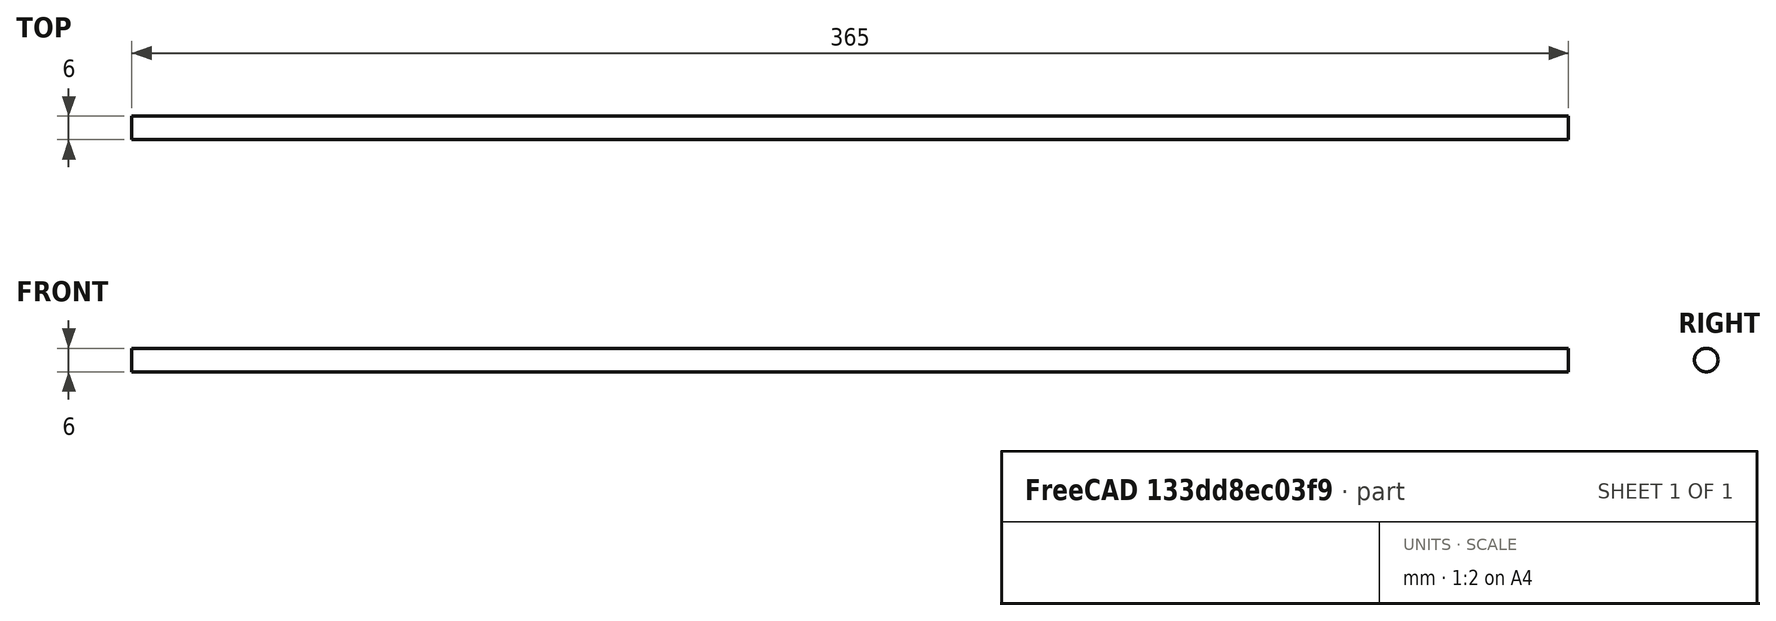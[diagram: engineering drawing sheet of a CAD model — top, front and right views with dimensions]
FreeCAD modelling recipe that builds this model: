
FCSTD DOCUMENT  (FreeCAD 0.18R15441 (Git))
Label: Rod_M6x365mm
License: All rights reserved
LicenseURL: http://en.wikipedia.org/wiki/All_rights_reserved
objects: Sketcher::SketchObject×1, PartDesign::Pad×1, PartDesign::Body×1, App::Part×1
note: 4 computed .brp shape members not serialized (recipe doc carries the construction recipe); baked Part::Feature solids carry a one-line shape summary decoded from their .brp

FEATURE [Sketcher::SketchObject] Sketch  label="RodSketch"
  MapMode = 5
  Placement = pos=(0,0,0) rot=(0.57735,0.57735,0.57735;2.0944rad)
  Support = -> [YZ_Plane001]
  sketch-geometry (1):
    g0: Circle CenterX=0 CenterY=0 CenterZ=0 NormalX=0 NormalY=0 NormalZ=1 AngleXU=0 Radius=3
  constraints (2):
    c: Coincident(g0,g-1)
    c: Radius(g0) = 3
FEATURE [PartDesign::Pad] Pad  label="RodPad"
  Length = 365
  Length2 = 100
  Midplane = true
  Placement = pos=(0,0,0) rot=(0.57735,0.57735,0.57735;2.0944rad)
  Profile = -> Sketch
  Type = 0
FEATURE [PartDesign::Body] Body  label="RodBody"
  Group = -> [Sketch,Pad]
  Origin = -> Origin001
  Tip = -> Pad
FEATURE [App::Part] Part  label="Rod_M6x365_Part"
  Group = -> [Body]
  License = CC BY 3.0
  LicenseURL = http://creativecommons.org/licenses/by/3.0/
  Origin = -> Origin
